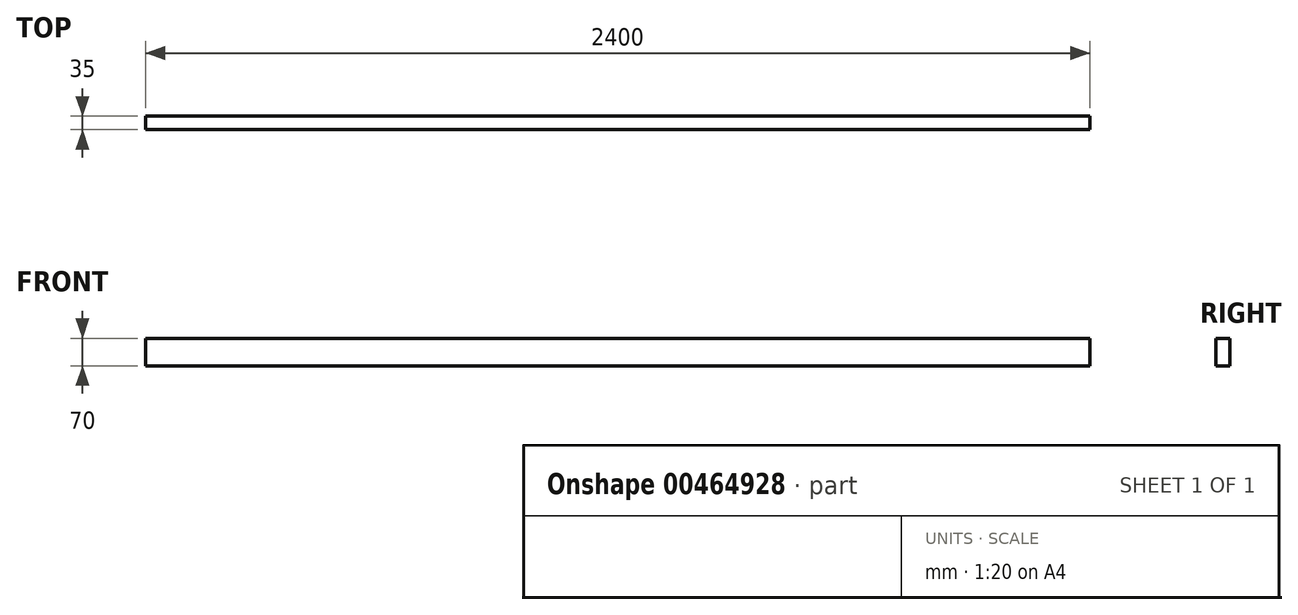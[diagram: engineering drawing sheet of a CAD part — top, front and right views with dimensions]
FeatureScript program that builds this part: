
annotation { "Feature Type Name" : "Feature", "Feature Type Description" : "" }
export const myFeature = defineFeature(function(context is Context, id is Id, definition is map)
    precondition{}
    {
        {
            var Q0;
            Q0=qCreatedBy(makeId("Right.planeOp"),FACE);
            var sketch = newSketch(context, id + "F0", { "sketchPlane" : qUnion([Q0])});
            skLineSegment(sketch, "E0.bottom", {"start": v(-17.5, 35) * mm, "end": v(17.5, 35) * mm});
            skLineSegment(sketch, "E0.top", {"start": v(-17.5, -35) * mm, "end": v(17.5, -35) * mm});
            skLineSegment(sketch, "E0.left", {"start": v(-17.5, 35) * mm, "end": v(-17.5, -35) * mm});
            skLineSegment(sketch, "E0.right", {"start": v(17.5, 35) * mm, "end": v(17.5, -35) * mm});
            skPoint(sketch, "E0.middle", {"position": v(0, 0) * mm});
            skSolve(sketch);
        }
        {
            var Q0;
            Q0=makeQuery(id+"F0.imprint","IMPRINT",FACE,{"disambiguationData":[TD([[makeQuery(id+"F0.imprint","IMPRINT",EDGE,{"derivedFrom":sQuery(id+"F0.wireOp",EDGE,"E0.bottom")}),-1.0]])]});
            extrude(context, id + "F1", {"entities" : qUnion([Q0]), "endBound" : BoundingType.SYMMETRIC, "depth" : 2400 * mm, "offsetDistance" : 25 * mm});
        }
    });
